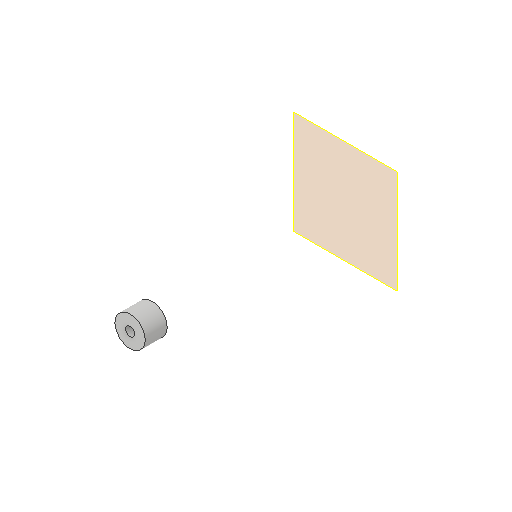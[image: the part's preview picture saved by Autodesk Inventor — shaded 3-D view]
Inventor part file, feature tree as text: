
AUTODESK INVENTOR PART (.ipt)
format: ipt  version: 2022 (Build 260153000, 153)  size: 87,040 bytes
history: native  units: mm
features: other x2, plane x1, extrude x1, sketch x1
ambient origin geometry x8: Origin, YZ Plane, XZ Plane, XY Plane, X Axis, Y Axis, Z Axis, Center Point
bodies: Solid1 (feature_tree)
feature tree (5):
  plane  "Work Plane1"
  extrude  "Extrusion1"  Depth=13.0mm
  sketch  "Sketch1"  dims[d0=5.5mm d1=18.0mm d2=13.0mm d3=0.0mm]
  other  "Assembly_Hi2_Uppsala_v3.iam"
  other  "Neje_puzzle_adapterplate_v3:3"
